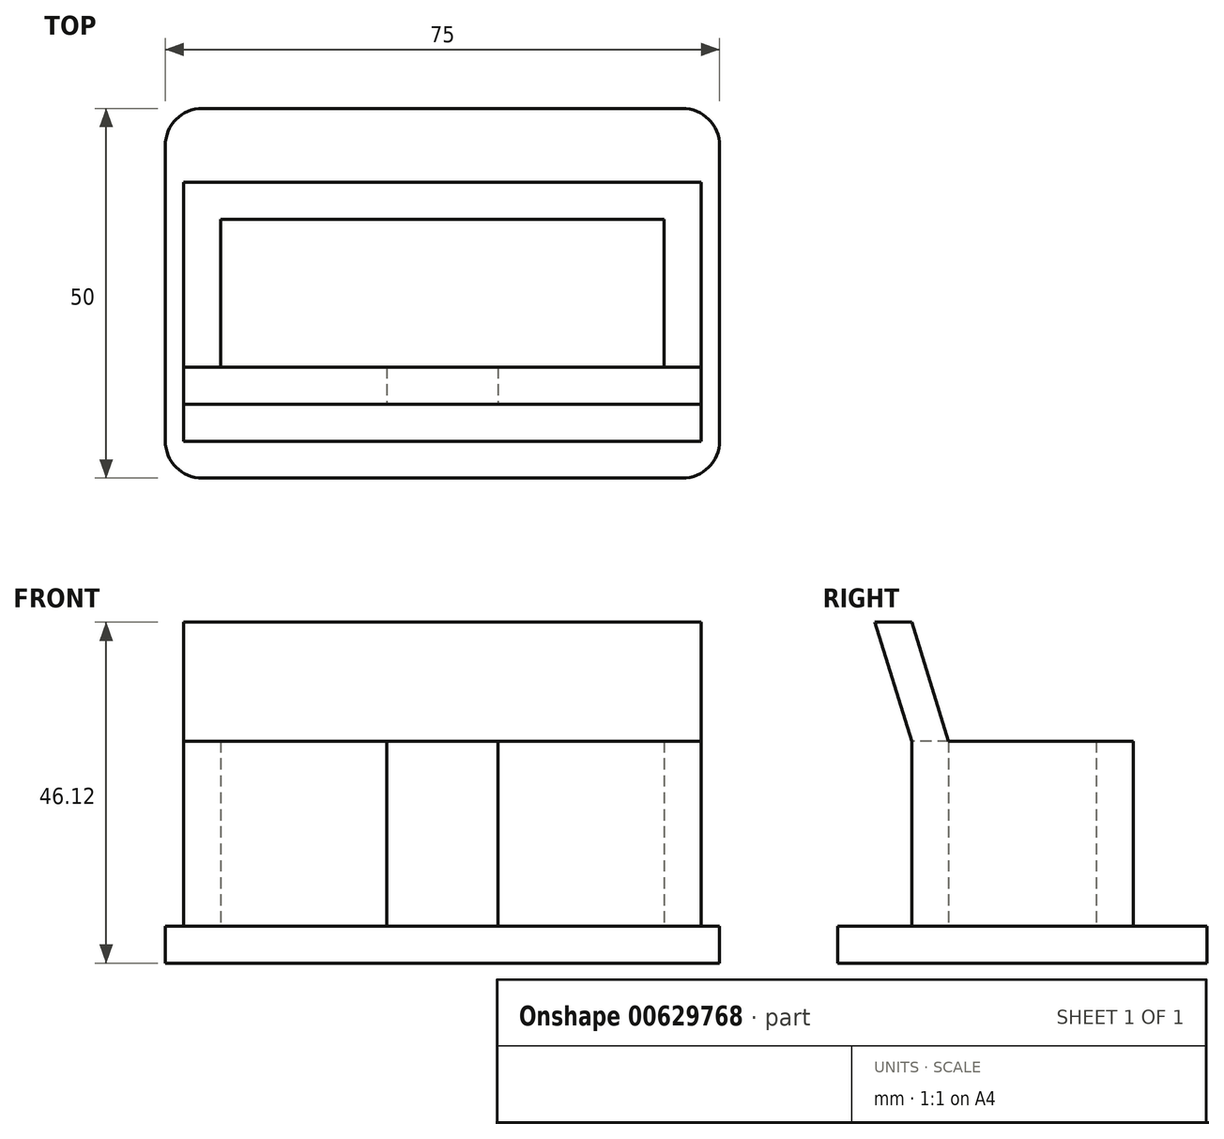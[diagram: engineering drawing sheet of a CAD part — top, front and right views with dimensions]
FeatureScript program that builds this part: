
annotation { "Feature Type Name" : "Feature", "Feature Type Description" : "" }
export const myFeature = defineFeature(function(context is Context, id is Id, definition is map)
    precondition{}
    {
        {
            var Q0;
            Q0=qCreatedBy(makeId("Top.planeOp"),FACE);
            var sketch = newSketch(context, id + "F0", { "sketchPlane" : qUnion([Q0])});
            skLineSegment(sketch, "E0.bottom", {"start": v(0, 0) * mm, "end": v(75, 0) * mm});
            skLineSegment(sketch, "E0.top", {"start": v(0, 50) * mm, "end": v(75, 50) * mm});
            skLineSegment(sketch, "E0.left", {"start": v(0, 0) * mm, "end": v(0, 50) * mm});
            skLineSegment(sketch, "E0.right", {"start": v(75, 0) * mm, "end": v(75, 50) * mm});
            skSolve(sketch);
        }
        {
            var Q0;
            Q0 = qSketchRegion(id + "F0", true);
            extrude(context, id + "F1", {"entities" : qUnion([Q0]), "depth" : 5 * mm, "offsetDistance" : 25 * mm});
        }
        {
            var Q0;
            Q0=makeQuery(id+"F1.opExtrude","SWEPT_EDGE",EDGE,{"disambiguationData":[OSD([sQuery(id+"F0.wireOp",EDGE,"E0.bottom"),sQuery(id+"F0.wireOp",EDGE,"E0.right")])]});
            var Q1;
            Q1=makeQuery(id+"F1.opExtrude","SWEPT_EDGE",EDGE,{"disambiguationData":[OSD([sQuery(id+"F0.wireOp",EDGE,"E0.bottom"),sQuery(id+"F0.wireOp",EDGE,"E0.left")])]});
            var Q2;
            Q2=makeQuery(id+"F1.opExtrude","SWEPT_EDGE",EDGE,{"disambiguationData":[OSD([sQuery(id+"F0.wireOp",EDGE,"E0.top"),sQuery(id+"F0.wireOp",EDGE,"E0.left")])]});
            var Q3;
            Q3=makeQuery(id+"F1.opExtrude","SWEPT_EDGE",EDGE,{"disambiguationData":[OSD([sQuery(id+"F0.wireOp",EDGE,"E0.top"),sQuery(id+"F0.wireOp",EDGE,"E0.right")])]});
            fillet(context, id + "F2", {"entities" : qUnion([Q0, Q1, Q2, Q3]), "radius" : 5 * mm, "tangentPropagation" : true, "allowEdgeOverflow" : false});
        }
        {
            var Q0;
            Q0=makeQuery(id+"F1.opExtrude","CAP_FACE",FACE,{"disambiguationData":[OSD([sQuery(id+"F0.wireOp",EDGE,"E0.bottom"),sQuery(id+"F0.wireOp",EDGE,"E0.top"),sQuery(id+"F0.wireOp",EDGE,"E0.left"),sQuery(id+"F0.wireOp",EDGE,"E0.right")])],"isStart":false});
            var sketch = newSketch(context, id + "F3", { "sketchPlane" : qUnion([Q0])});
            skLineSegment(sketch, "E1.bottom", {"start": v(2.5, 10) * mm, "end": v(30, 10) * mm});
            skLineSegment(sketch, "E1.top", {"start": v(2.5, 40) * mm, "end": v(72.5, 40) * mm});
            skLineSegment(sketch, "E1.left", {"start": v(2.5, 10) * mm, "end": v(2.5, 40) * mm});
            skLineSegment(sketch, "E1.right", {"start": v(72.5, 10) * mm, "end": v(72.5, 40) * mm});
            skLineSegment(sketch, "E2.bottom", {"start": v(7.5, 35) * mm, "end": v(67.5, 35) * mm});
            skLineSegment(sketch, "E2.top", {"start": v(7.5, 15) * mm, "end": v(30, 15) * mm});
            skLineSegment(sketch, "E2.left", {"start": v(7.5, 35) * mm, "end": v(7.5, 15) * mm});
            skLineSegment(sketch, "E2.right", {"start": v(67.5, 35) * mm, "end": v(67.5, 15) * mm});
            skLineSegment(sketch, "E3", {"start": v(30, 15) * mm, "end": v(30, 10) * mm});
            skLineSegment(sketch, "E4", {"start": v(45, 15) * mm, "end": v(45, 10) * mm});
            skLineSegment(sketch, "E5.trimOffspring", {"start": v(45, 15) * mm, "end": v(67.5, 15) * mm});
            skLineSegment(sketch, "E6.trimOffspring", {"start": v(45, 10) * mm, "end": v(72.5, 10) * mm});
            skSolve(sketch);
        }
        {
            var Q0;
            Q0 = qSketchRegion(id + "F3", true);
            extrude(context, id + "F4", {"entities" : qUnion([Q0]), "operationType" : NewBodyOperationType.ADD, "depth" : 25 * mm, "offsetDistance" : 25 * mm});
        }
        {
            var Q0;
            Q0=makeQuery(id+"F4.opExtrude","SWEPT_FACE",FACE,{"disambiguationData":[OSD([sQuery(id+"F3.wireOp",EDGE,"E1.left")])]});
            var sketch = newSketch(context, id + "F5", { "sketchPlane" : qUnion([Q0])});
            skLineSegment(sketch, "E7", {"start": v(-10, 30) * mm, "end": v(-5, 46.12) * mm});
            skLineSegment(sketch, "E8", {"start": v(-5, 46.12) * mm, "end": v(-10, 46.12) * mm});
            skLineSegment(sketch, "E9", {"start": v(-10, 46.12) * mm, "end": v(-15, 30) * mm});
            skSolve(sketch);
        }
        {
            var Q0;
            {var subQ0=sQuery(id+"F5.wireOp",EDGE,"E7");Q0=makeQuery(id+"F5.imprint","IMPRINT",FACE,{"disambiguationData":[TD([[makeQuery(id+"F5.imprint","IMPRINT",EDGE,{"derivedFrom":subQ0}),1.0]])]});}
            extrude(context, id + "F6", {"entities" : qUnion([Q0]), "operationType" : NewBodyOperationType.ADD, "oppositeDirection" : true, "depth" : 70 * mm, "offsetDistance" : 25 * mm});
        }
    });
